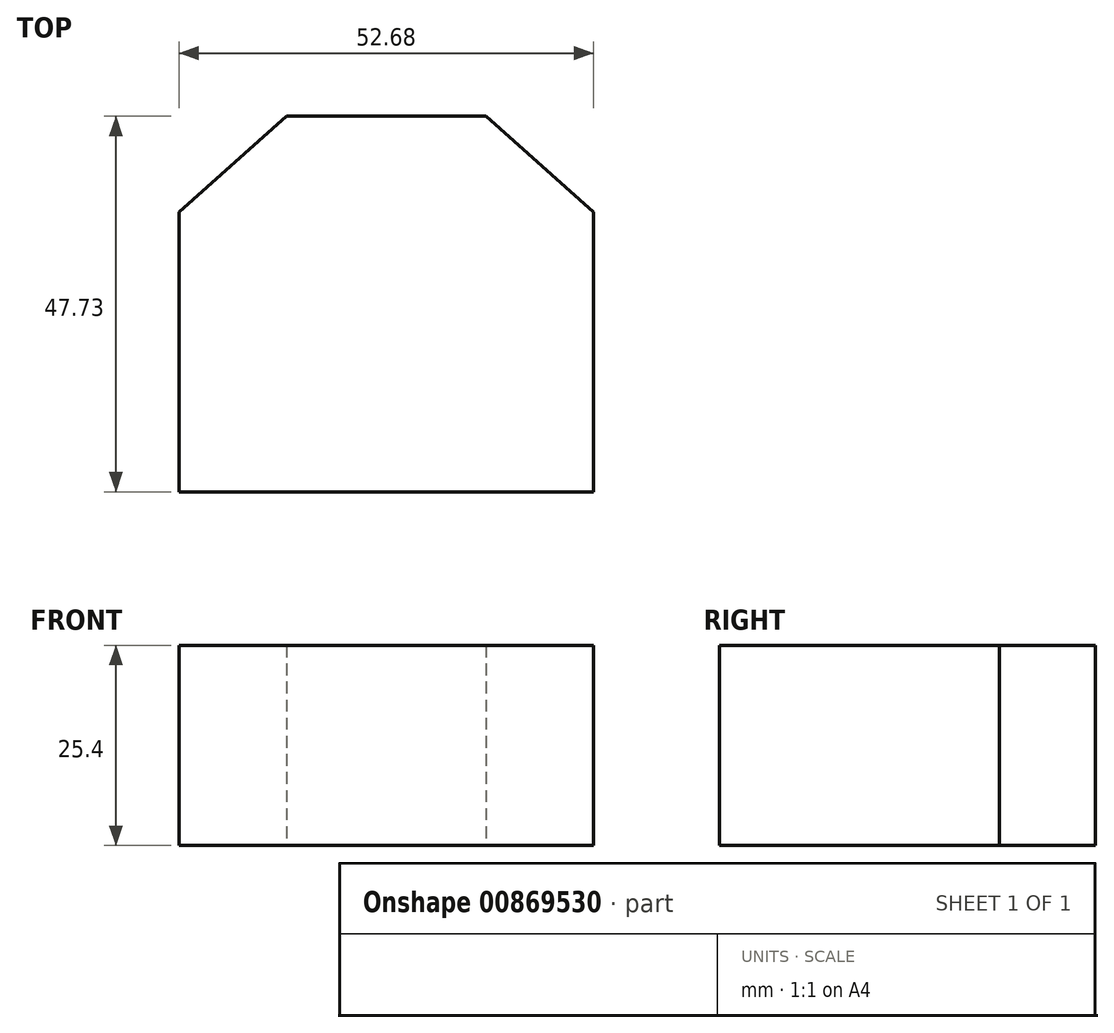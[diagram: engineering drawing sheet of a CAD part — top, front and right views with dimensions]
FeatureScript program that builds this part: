
annotation { "Feature Type Name" : "Feature", "Feature Type Description" : "" }
export const myFeature = defineFeature(function(context is Context, id is Id, definition is map)
    precondition{}
    {
        {
            var Q0;
            Q0=qCreatedBy(makeId("Top.planeOp"),FACE);
            var sketch = newSketch(context, id + "F0", { "sketchPlane" : qUnion([Q0])});
            skLineSegment(sketch, "E0", {"start": v(-26.34, 15.3) * mm, "end": v(-26.34, -20.26) * mm});
            skLineSegment(sketch, "E1", {"start": v(-26.34, -20.26) * mm, "end": v(0, -20.26) * mm});
            skLineSegment(sketch, "E2", {"start": v(-26.34, 15.3) * mm, "end": v(-12.68, 27.47) * mm});
            skLineSegment(sketch, "E3", {"start": v(-12.68, 27.47) * mm, "end": v(0, 27.47) * mm});
            skLineSegment(sketch, "E4", {"start": v(-12.68, 27.47) * mm, "end": v(-12.68, -20.26) * mm});
            skPoint(sketch, "E4.endSnap0", {"position": v(-13.17, -20.26) * mm});
            skLineSegment(sketch, "E5.MirrorCS", {"start": v(12.68, 27.47) * mm, "end": v(0, 27.47) * mm});
            skLineSegment(sketch, "E6.MirrorCS", {"start": v(12.68, 27.47) * mm, "end": v(12.68, -20.26) * mm});
            skLineSegment(sketch, "E7.MirrorCS", {"start": v(26.34, 15.3) * mm, "end": v(12.68, 27.47) * mm});
            skLineSegment(sketch, "E8.MirrorCS", {"start": v(26.34, 15.3) * mm, "end": v(26.34, -20.26) * mm});
            skLineSegment(sketch, "E9.MirrorCS", {"start": v(26.34, -20.26) * mm, "end": v(0, -20.26) * mm});
            skSolve(sketch);
        }
        {
            var Q0;
            Q0 = qSketchRegion(id + "F0", true);
            extrude(context, id + "F1", {"entities" : qUnion([Q0]), "depth" : 25.4 * mm, "offsetDistance" : 25.4 * mm});
        }
    });
